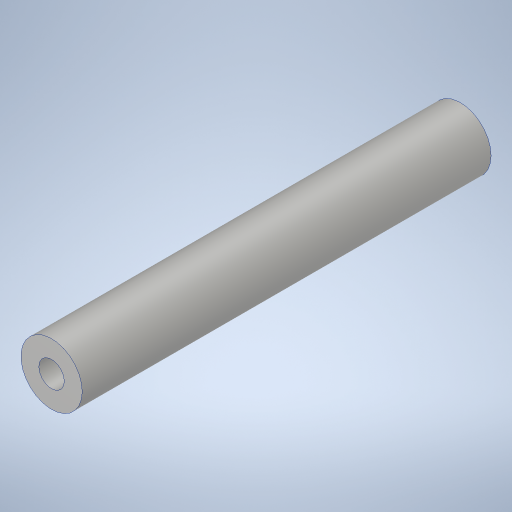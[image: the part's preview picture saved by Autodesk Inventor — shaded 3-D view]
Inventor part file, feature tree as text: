
AUTODESK INVENTOR PART (.ipt)
format: ipt  version: 2023.4 (Build 274418000, 418)  size: 243,200 bytes
history: native  units: in
note: dims shown in document units (in); Inventor stores cm internally (conversion verified against a paired STEP export)
features: extrude x1, hole x1
ambient origin geometry x8: Origin, YZ Plane, XZ Plane, XY Plane, X Axis, Y Axis, Z Axis, Center Point
bodies: Solid1 (feature_tree)
feature tree (2):
  extrude  "Extrusion1"  Depth=2.5in
  hole  "Hole1"  [1 undecoded]
note: 1 required parameter value undecoded (feature->parameter linkage not recoverable at this tier; creation-order binding heuristic only, values carry confidence <= 0.55)
